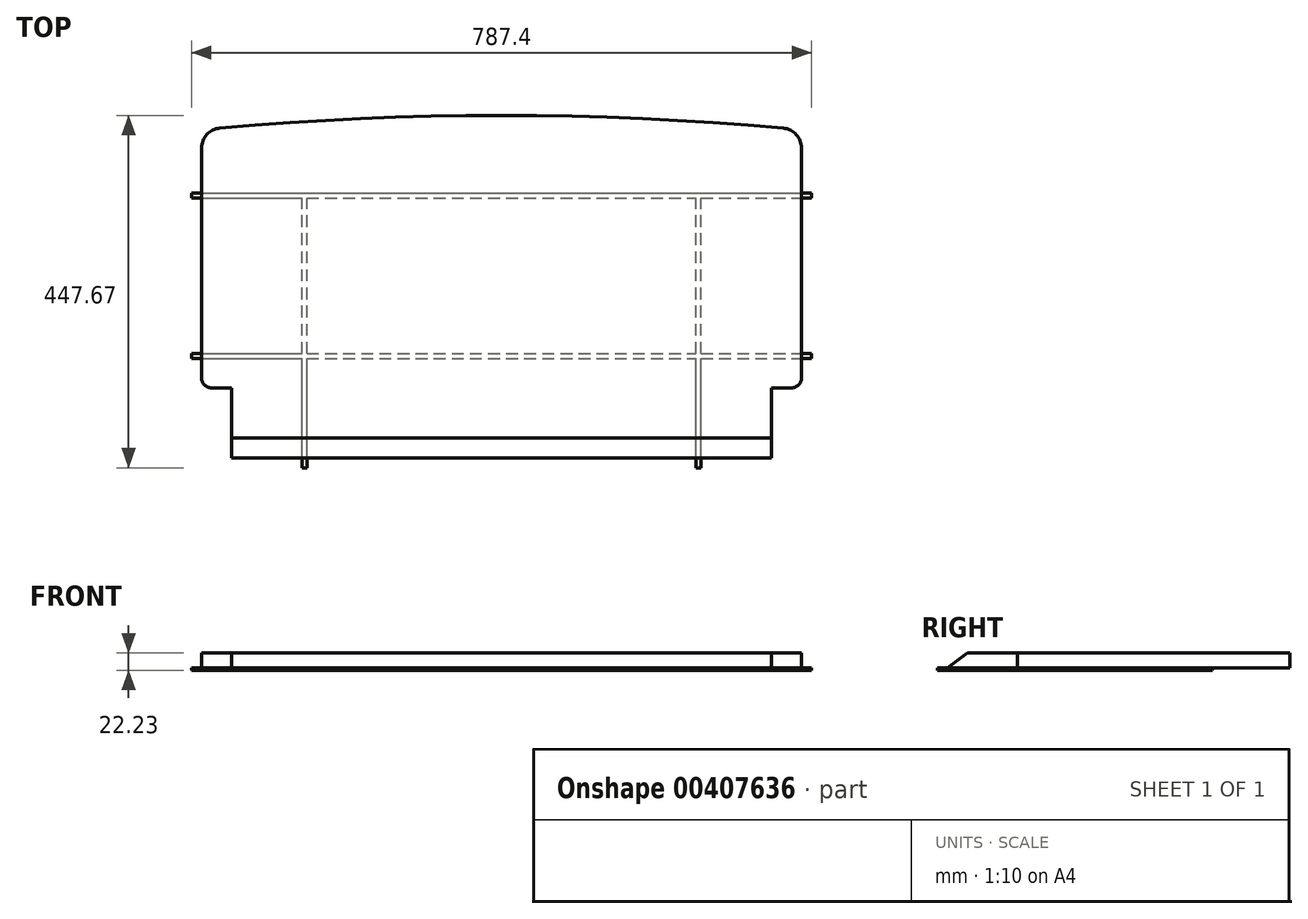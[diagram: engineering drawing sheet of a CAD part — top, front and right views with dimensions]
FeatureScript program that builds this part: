
annotation { "Feature Type Name" : "Feature", "Feature Type Description" : "" }
export const myFeature = defineFeature(function(context is Context, id is Id, definition is map)
    precondition{}
    {
        {
            var Q0;
            Q0=qCreatedBy(makeId("Top.planeOp"),FACE);
            var sketch = newSketch(context, id + "F0", { "sketchPlane" : qUnion([Q0])});
            skLineSegment(sketch, "E0.bottom", {"start": v(38.1, 0) * mm, "end": v(723.9, 0) * mm});
            skLineSegment(sketch, "E0.top", {"start": v(0, 393.7) * mm, "end": v(762, 393.7) * mm, "construction": true});
            skLineSegment(sketch, "E0.left", {"start": v(0, 101.6) * mm, "end": v(0, 393.7) * mm});
            skLineSegment(sketch, "E0.right", {"start": v(762, 101.6) * mm, "end": v(762, 393.7) * mm});
            skLineSegment(sketch, "E1", {"start": v(38.1, 0) * mm, "end": v(38.1, 88.9) * mm});
            skLineSegment(sketch, "E2", {"start": v(38.1, 88.9) * mm, "end": v(723.9, 88.9) * mm, "construction": true});
            skLineSegment(sketch, "E3", {"start": v(723.9, 88.9) * mm, "end": v(723.9, 0) * mm});
            skLineSegment(sketch, "E4", {"start": v(723.9, 25.4) * mm, "end": v(38.1, 25.4) * mm, "construction": true});
            skLineSegment(sketch, "E5", {"start": v(38.1, 88.9) * mm, "end": v(12.7, 88.9) * mm});
            skLineSegment(sketch, "E6", {"start": v(723.9, 88.9) * mm, "end": v(749.3, 88.9) * mm});
            skArc(sketch, "E7", {"start": v(23.14, 419) * mm, "mid": v(6.66, 410.84) * mm, "end": v(0, 393.7) * mm});
            skArc(sketch, "E8", {"start": v(762, 393.7) * mm, "mid": v(755.34, 410.84) * mm, "end": v(738.86, 419) * mm});
            skArc(sketch, "E9", {"start": v(738.86, 419) * mm, "mid": v(381, 434.97) * mm, "end": v(23.14, 419) * mm});
            skPoint(sketch, "E10.visualSharp", {"position": v(0, 88.9) * mm});
            skArc(sketch, "E10.filletArc", {"start": v(0, 101.6) * mm, "mid": v(3.72, 92.62) * mm, "end": v(12.7, 88.9) * mm});
            skPoint(sketch, "E11.visualSharp", {"position": v(762, 88.9) * mm});
            skArc(sketch, "E11.filletArc", {"start": v(749.3, 88.9) * mm, "mid": v(758.28, 92.62) * mm, "end": v(762, 101.6) * mm});
            skLineSegment(sketch, "E12", {"start": v(381, 0) * mm, "end": v(381, 434.98) * mm, "construction": true});
            skSolve(sketch);
        }
        {
            var Q0;
            Q0=makeQuery(id+"F0.imprint","IMPRINT",FACE,{"disambiguationData":[TD([[makeQuery(id+"F0.imprint","IMPRINT",EDGE,{"derivedFrom":sQuery(id+"F0.wireOp",EDGE,"E0.bottom")}),1.0]])]});
            extrude(context, id + "F1", {"entities" : qUnion([Q0]), "oppositeDirection" : true, "depth" : 19.05 * mm});
        }
        {
            var Q0;
            Q0=makeQuery(id+"F1.opExtrude","SWEPT_FACE",FACE,{"disambiguationData":[OSD([sQuery(id+"F0.wireOp",EDGE,"E1")])]});
            var sketch = newSketch(context, id + "F2", { "sketchPlane" : qUnion([Q0])});
            skPoint(sketch, "E13.0", {"position": v(-25.4, 0) * mm});
            skPoint(sketch, "E14.0", {"position": v(0, 0) * mm});
            skPoint(sketch, "E15.0", {"position": v(0, -19.05) * mm});
            skLineSegment(sketch, "E16", {"start": v(-25.4, 0) * mm, "end": v(0, -19.05) * mm});
            skLineSegment(sketch, "E17", {"start": v(0, 0) * mm, "end": v(-25.4, 0) * mm});
            skLineSegment(sketch, "E18", {"start": v(0, -19.05) * mm, "end": v(0, 0) * mm});
            skSolve(sketch);
        }
        {
            var Q0;
            Q0=makeQuery(id+"F2.imprint","IMPRINT",FACE,{"disambiguationData":[TD([[makeQuery(id+"F2.imprint","IMPRINT",EDGE,{"derivedFrom":sQuery(id+"F2.wireOp",EDGE,"E16")}),1.0]])]});
            extrude(context, id + "F3", {"entities" : qUnion([Q0]), "operationType" : NewBodyOperationType.REMOVE, "endBound" : BoundingType.THROUGH_ALL, "oppositeDirection" : true, "depth" : 25.4 * mm});
        }
        {
            var Q0;
            Q0=makeQuery(id+"F1.opExtrude","CAP_FACE",FACE,{"disambiguationData":[OSD([sQuery(id+"F0.wireOp",EDGE,"E0.bottom"),sQuery(id+"F0.wireOp",EDGE,"E0.left"),sQuery(id+"F0.wireOp",EDGE,"E0.right"),sQuery(id+"F0.wireOp",EDGE,"E1"),sQuery(id+"F0.wireOp",EDGE,"E3"),sQuery(id+"F0.wireOp",EDGE,"E5"),sQuery(id+"F0.wireOp",EDGE,"E6"),sQuery(id+"F0.wireOp",EDGE,"E7"),sQuery(id+"F0.wireOp",EDGE,"E8"),sQuery(id+"F0.wireOp",EDGE,"E9"),sQuery(id+"F0.wireOp",EDGE,"E10.filletArc"),sQuery(id+"F0.wireOp",EDGE,"E11.filletArc")])],"isStart":false});
            extrude(context, id + "F4", {"entities" : qUnion([Q0]), "depth" : 1 / 203.2 * mm, "offsetDistance" : 25.4 * mm});
        }
        {
            var Q0;
            Q0=makeQuery(id+"F1.opExtrude","CAP_FACE",FACE,{"disambiguationData":[OSD([sQuery(id+"F0.wireOp",EDGE,"E0.bottom"),sQuery(id+"F0.wireOp",EDGE,"E0.left"),sQuery(id+"F0.wireOp",EDGE,"E0.right"),sQuery(id+"F0.wireOp",EDGE,"E1"),sQuery(id+"F0.wireOp",EDGE,"E3"),sQuery(id+"F0.wireOp",EDGE,"E5"),sQuery(id+"F0.wireOp",EDGE,"E6"),sQuery(id+"F0.wireOp",EDGE,"E7"),sQuery(id+"F0.wireOp",EDGE,"E8"),sQuery(id+"F0.wireOp",EDGE,"E9"),sQuery(id+"F0.wireOp",EDGE,"E10.filletArc"),sQuery(id+"F0.wireOp",EDGE,"E11.filletArc")])],"isStart":false});
            var sketch = newSketch(context, id + "F5", { "sketchPlane" : qUnion([Q0])});
            skLineSegment(sketch, "E19.bottom", {"start": v(-12.7, -126.05) * mm, "end": v(774.7, -126.05) * mm});
            skLineSegment(sketch, "E19.top", {"start": v(-12.7, -132.4) * mm, "end": v(774.7, -132.4) * mm});
            skLineSegment(sketch, "E19.left", {"start": v(-12.7, -126.05) * mm, "end": v(-12.7, -132.4) * mm});
            skLineSegment(sketch, "E19.right", {"start": v(774.7, -126.05) * mm, "end": v(774.7, -132.4) * mm});
            skLineSegment(sketch, "E20.bottom", {"start": v(-12.7, -330.2) * mm, "end": v(774.7, -330.2) * mm});
            skLineSegment(sketch, "E20.top", {"start": v(-12.7, -336.56) * mm, "end": v(774.7, -336.56) * mm});
            skLineSegment(sketch, "E20.left", {"start": v(-12.7, -330.2) * mm, "end": v(-12.7, -336.56) * mm});
            skLineSegment(sketch, "E20.right", {"start": v(774.7, -330.2) * mm, "end": v(774.7, -336.56) * mm});
            skPoint(sketch, "E21", {"position": v(762, -330.2) * mm});
            skPoint(sketch, "E22", {"position": v(0, -330.2) * mm});
            skLineSegment(sketch, "E23.bottom", {"start": v(127.54, 12.7) * mm, "end": v(133.89, 12.7) * mm});
            skLineSegment(sketch, "E23.top", {"start": v(127.54, -330.2) * mm, "end": v(133.89, -330.2) * mm});
            skLineSegment(sketch, "E23.left", {"start": v(127.54, 12.7) * mm, "end": v(127.54, -330.2) * mm});
            skLineSegment(sketch, "E23.right", {"start": v(133.89, 12.7) * mm, "end": v(133.89, -330.2) * mm});
            skLineSegment(sketch, "E24.bottom", {"start": v(628.11, 12.7) * mm, "end": v(634.46, 12.7) * mm});
            skLineSegment(sketch, "E24.top", {"start": v(628.11, -330.2) * mm, "end": v(634.46, -330.2) * mm});
            skLineSegment(sketch, "E24.left", {"start": v(628.11, 12.7) * mm, "end": v(628.11, -330.2) * mm});
            skLineSegment(sketch, "E24.right", {"start": v(634.46, 12.7) * mm, "end": v(634.46, -330.2) * mm});
            skLineSegment(sketch, "E25", {"start": v(133.89, 12.7) * mm, "end": v(628.11, 12.7) * mm, "construction": true});
            skPoint(sketch, "E26", {"position": v(381, 12.7) * mm});
            skSolve(sketch);
        }
        {
            var Q0;
            Q0 = qSketchRegion(id + "F5", true);
            extrude(context, id + "F6", {"entities" : qUnion([Q0]), "operationType" : NewBodyOperationType.ADD, "depth" : 3.17 * mm, "offsetDistance" : 25.4 * mm});
        }
    });
